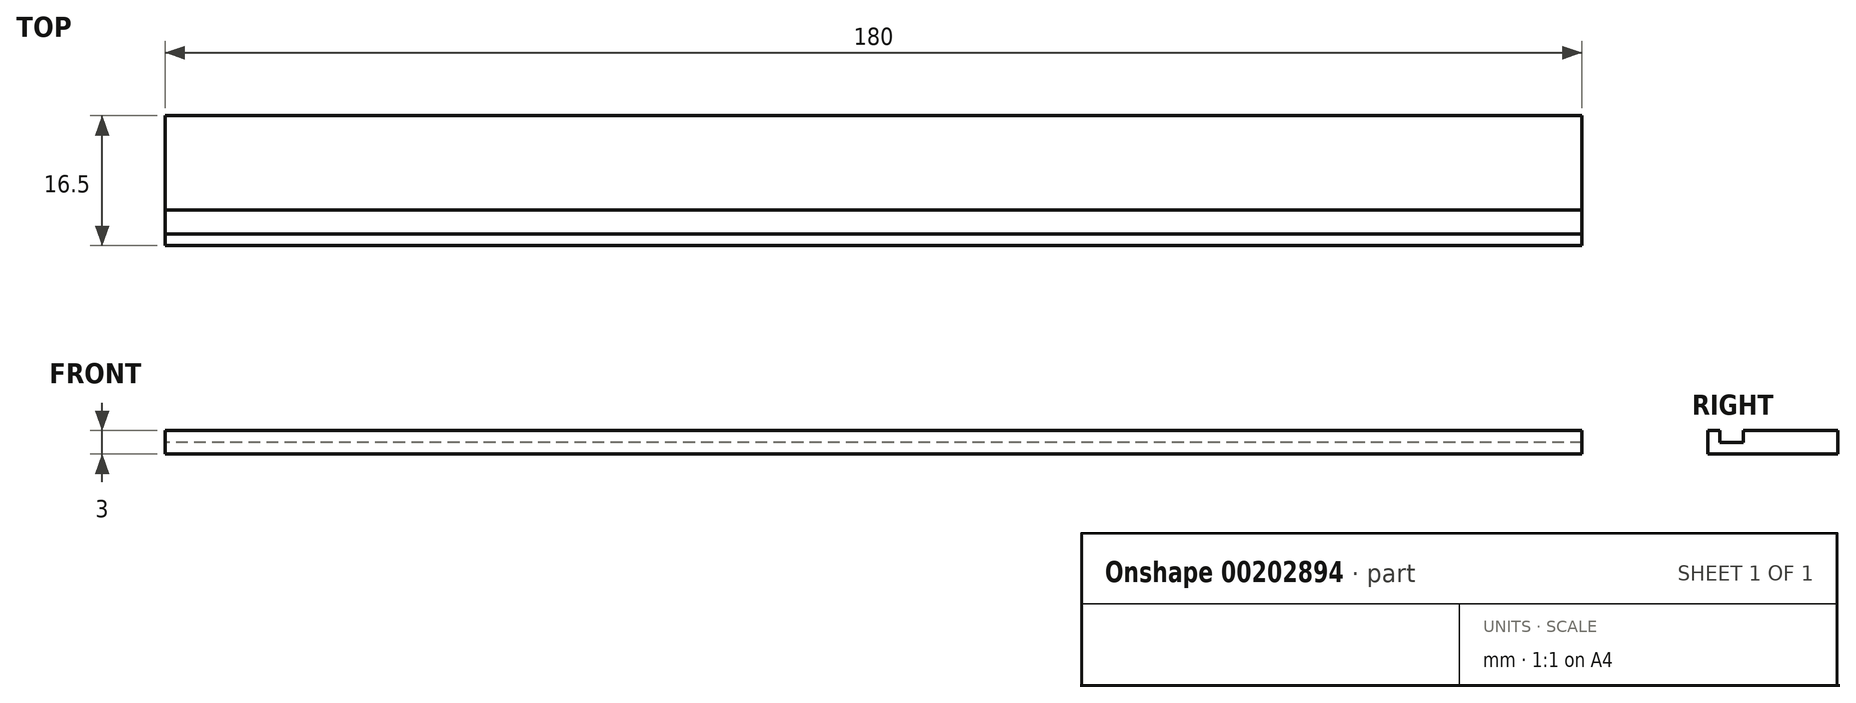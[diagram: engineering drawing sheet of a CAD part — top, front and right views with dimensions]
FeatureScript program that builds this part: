
annotation { "Feature Type Name" : "Feature", "Feature Type Description" : "" }
export const myFeature = defineFeature(function(context is Context, id is Id, definition is map)
    precondition{}
    {
        {
            var Q0;
            Q0=qCreatedBy(makeId("Right.planeOp"),FACE);
            var sketch = newSketch(context, id + "F0", { "sketchPlane" : qUnion([Q0])});
            skLineSegment(sketch, "E0", {"start": v(-4.63, 0) * mm, "end": v(7.64, 0) * mm, "construction": true});
            skLineSegment(sketch, "E1", {"start": v(0, 6.92) * mm, "end": v(0, -6.64) * mm, "construction": true});
            skLineSegment(sketch, "E2", {"start": v(-3, 3) * mm, "end": v(-3, 0) * mm});
            skLineSegment(sketch, "E3", {"start": v(-3, 0) * mm, "end": v(0, 0) * mm});
            skLineSegment(sketch, "E4", {"start": v(-3, 3) * mm, "end": v(-1.5, 3) * mm});
            skLineSegment(sketch, "E5", {"start": v(-1.5, 3) * mm, "end": v(-1.5, 1.5) * mm});
            skLineSegment(sketch, "E6", {"start": v(-1.5, 1.5) * mm, "end": v(0, 1.5) * mm});
            skLineSegment(sketch, "E7.MirrorCS", {"start": v(1.5, 3) * mm, "end": v(1.5, 1.5) * mm});
            skLineSegment(sketch, "E8.MirrorCS", {"start": v(1.5, 1.5) * mm, "end": v(0, 1.5) * mm});
            skLineSegment(sketch, "E9.MirrorCS", {"start": v(3, 3) * mm, "end": v(1.5, 3) * mm});
            skLineSegment(sketch, "E10.MirrorCS", {"start": v(3, 0) * mm, "end": v(0, 0) * mm});
            skLineSegment(sketch, "E11", {"start": v(3, 0) * mm, "end": v(13.5, 0) * mm});
            skLineSegment(sketch, "E12", {"start": v(13.5, 0) * mm, "end": v(13.5, 3) * mm});
            skLineSegment(sketch, "E13", {"start": v(13.5, 3) * mm, "end": v(3, 3) * mm});
            skSolve(sketch);
        }
        {
            var Q0;
            Q0 = qSketchRegion(id + "F0", true);
            extrude(context, id + "F1", {"entities" : qUnion([Q0]), "depth" : 180 * mm});
        }
    });
